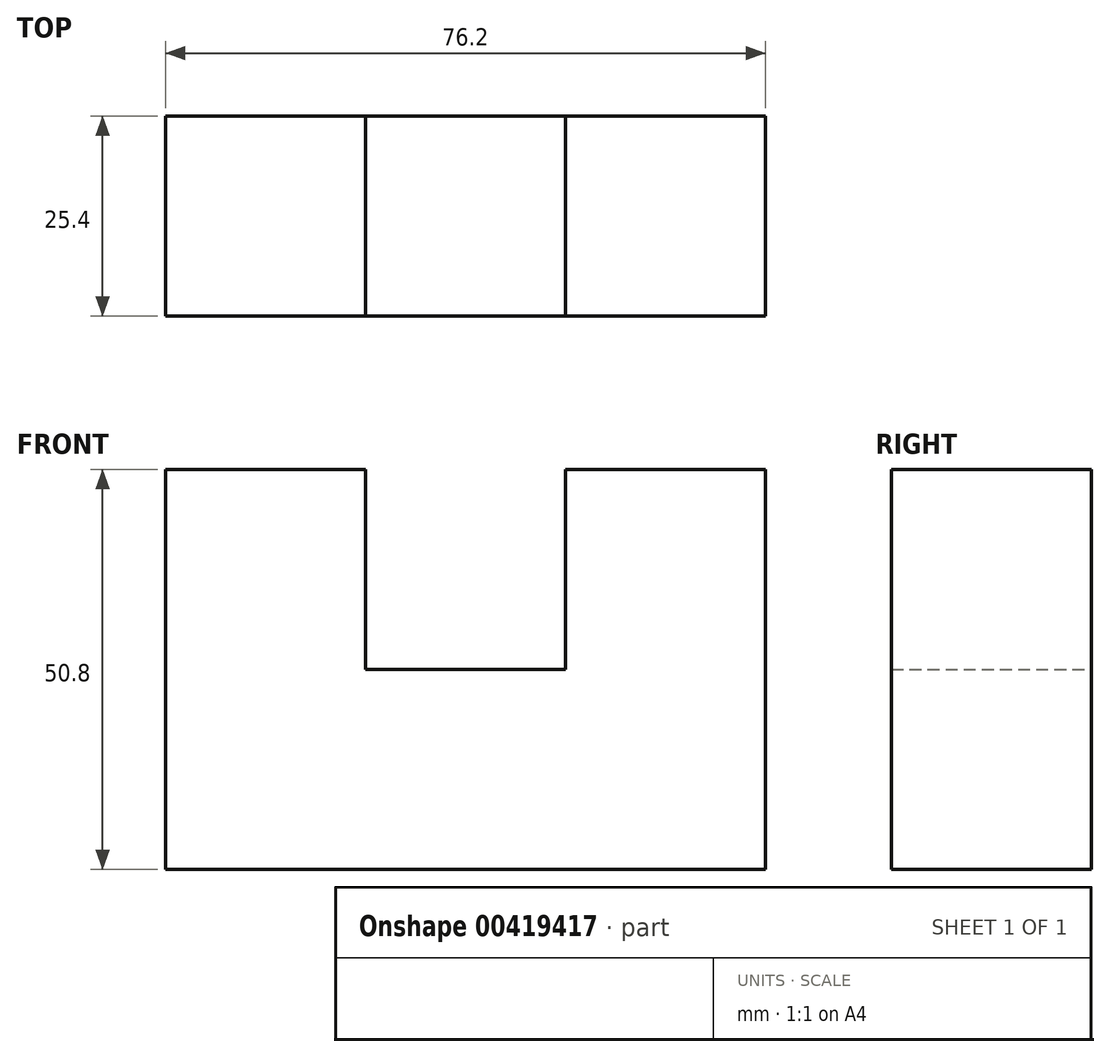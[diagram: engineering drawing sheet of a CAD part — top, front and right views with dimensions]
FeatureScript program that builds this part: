
annotation { "Feature Type Name" : "Feature", "Feature Type Description" : "" }
export const myFeature = defineFeature(function(context is Context, id is Id, definition is map)
    precondition{}
    {
        {
            var Q0;
            Q0=qCreatedBy(makeId("Front.planeOp"),FACE);
            var sketch = newSketch(context, id + "F0", { "sketchPlane" : qUnion([Q0])});
            skLineSegment(sketch, "E0", {"start": v(-52.9, 62.25) * mm, "end": v(-52.9, 11.45) * mm});
            skLineSegment(sketch, "E1", {"start": v(-52.9, 62.25) * mm, "end": v(-27.5, 62.25) * mm});
            skLineSegment(sketch, "E2", {"start": v(-27.5, 62.25) * mm, "end": v(-27.5, 36.85) * mm});
            skLineSegment(sketch, "E3", {"start": v(-27.5, 36.85) * mm, "end": v(-2.1, 36.85) * mm});
            skLineSegment(sketch, "E4", {"start": v(-2.1, 36.85) * mm, "end": v(-2.1, 62.25) * mm});
            skLineSegment(sketch, "E5", {"start": v(-2.1, 62.25) * mm, "end": v(23.3, 62.25) * mm});
            skLineSegment(sketch, "E6", {"start": v(23.3, 62.25) * mm, "end": v(23.3, 11.45) * mm});
            skLineSegment(sketch, "E7", {"start": v(23.3, 11.45) * mm, "end": v(-52.9, 11.45) * mm});
            skSolve(sketch);
        }
        {
            var Q0;
            Q0 = qSketchRegion(id + "F0", true);
            extrude(context, id + "F1", {"entities" : qUnion([Q0]), "depth" : 25.4 * mm});
        }
    });
